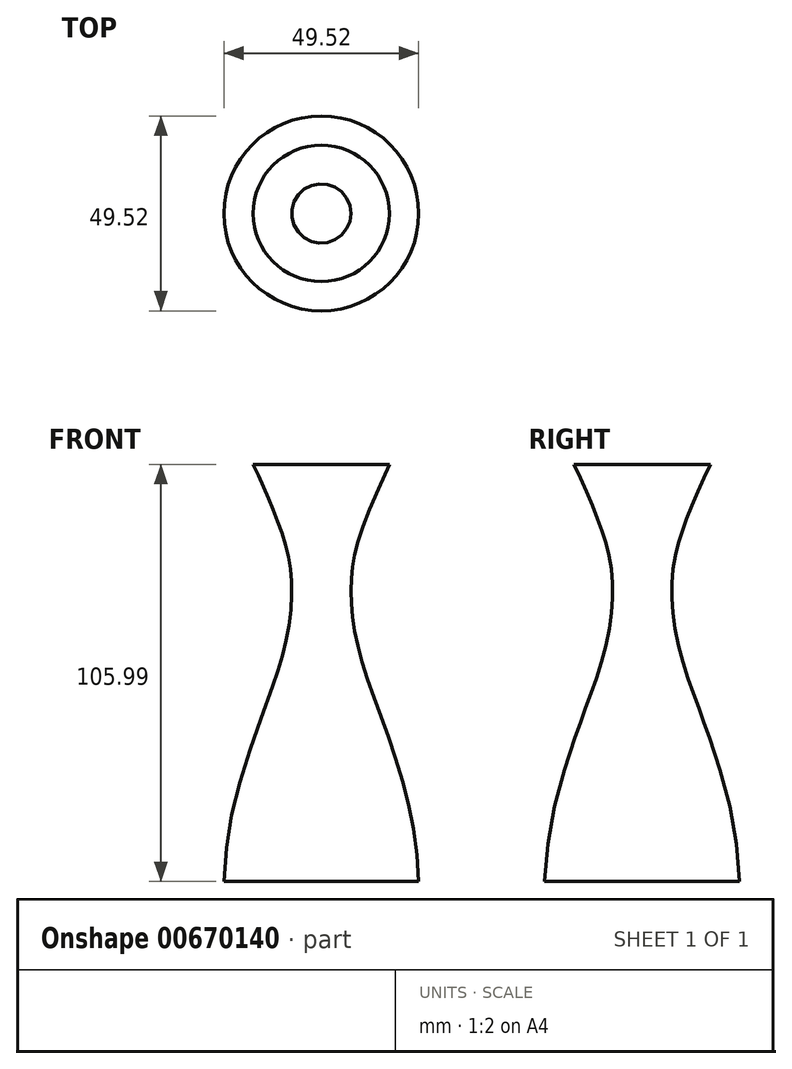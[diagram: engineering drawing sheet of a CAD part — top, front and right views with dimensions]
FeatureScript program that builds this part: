
annotation { "Feature Type Name" : "Feature", "Feature Type Description" : "" }
export const myFeature = defineFeature(function(context is Context, id is Id, definition is map)
    precondition{}
    {
        {
            var Q0;
            Q0=qCreatedBy(makeId("Front.planeOp"),FACE);
            var sketch = newSketch(context, id + "F0", { "sketchPlane" : qUnion([Q0])});
            skLineSegment(sketch, "E0", {"start": v(0, 0) * mm, "end": v(0, 105.76) * mm});
            skSolve(sketch);
        }
        {
            var Q0;
            Q0=qCreatedBy(makeId("Front.planeOp"),FACE);
            var sketch = newSketch(context, id + "F1", { "sketchPlane" : qUnion([Q0])});
            skFitSpline(sketch, "E1", {"points": [v(17.32, 106) * mm, v(7.58, 76.23) * mm, v(10.73, 54.48) * mm, v(24.76, 0) * mm], "startDerivative": vector(-72.13, -155.35) * mm, "endDerivative": vector(4.07, -159.5) * mm});
            skSolve(sketch);
        }
        {
            var Q0;
            Q0 = qSketchRegion(id + "F1", true);
            var Q1;
            Q1=sQuery(id+"F1.wireOp",EDGE,"E1");
            var Q2;
            Q2=sQuery(id+"F0.wireOp",EDGE,"E0");
            revolve(context, id + "F2", {"bodyType" : ToolBodyType.SURFACE, "entities" : qUnion([Q0]), "surfaceEntities" : qUnion([Q1]), "axis" : qUnion([Q2]), "revolveType" : RevolveType.FULL});
        }
    });
